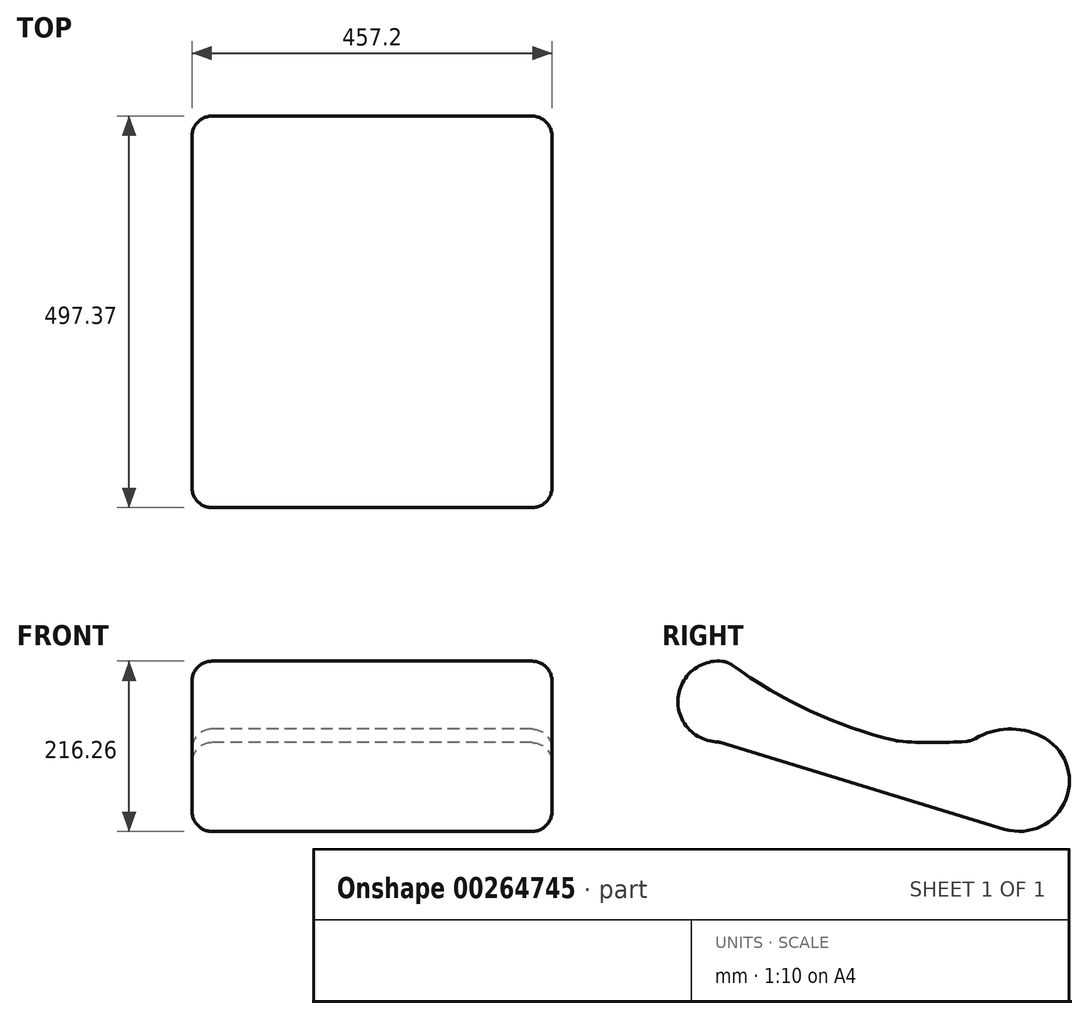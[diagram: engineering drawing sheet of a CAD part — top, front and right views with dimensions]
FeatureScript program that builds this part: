
annotation { "Feature Type Name" : "Feature", "Feature Type Description" : "" }
export const myFeature = defineFeature(function(context is Context, id is Id, definition is map)
    precondition{}
    {
        {
            var Q0;
            Q0=qCreatedBy(makeId("Right.planeOp"),FACE);
            var sketch = newSketch(context, id + "F0", { "sketchPlane" : qUnion([Q0])});
            skLineSegment(sketch, "E0", {"start": v(-410.9, 125.23) * mm, "end": v(-46.45, 14.16) * mm});
            skArc(sketch, "E1", {"start": v(-46.45, 14.16) * mm, "mid": v(31.4, 51.79) * mm, "end": v(0, 132.36) * mm});
            skArc(sketch, "E2", {"start": v(0, 132.36) * mm, "mid": v(-45.23, 141.16) * mm, "end": v(-88.83, 126.26) * mm});
            skArc(sketch, "E3", {"start": v(-183.23, 126.26) * mm, "mid": v(-136.03, 124.16) * mm, "end": v(-88.83, 126.26) * mm});
            skArc(sketch, "E4", {"start": v(-397.28, 225.96) * mm, "mid": v(-295.26, 165.36) * mm, "end": v(-183.23, 126.26) * mm});
            skArc(sketch, "E5", {"start": v(-397.28, 225.96) * mm, "mid": v(-461.09, 183.3) * mm, "end": v(-410.9, 125.23) * mm});
            skSolve(sketch);
        }
        {
            var Q0;
            Q0 = qSketchRegion(id + "F0", true);
            extrude(context, id + "F1", {"entities" : qUnion([Q0]), "endBound" : BoundingType.SYMMETRIC, "depth" : 457.2 * mm});
        }
        {
            var Q0;
            Q0=makeQuery(id+"F1.opExtrude","CAP_FACE",FACE,{"disambiguationData":[OSD([sQuery(id+"F0.wireOp",EDGE,"E0"),sQuery(id+"F0.wireOp",EDGE,"E1"),sQuery(id+"F0.wireOp",EDGE,"E2"),sQuery(id+"F0.wireOp",EDGE,"E3"),sQuery(id+"F0.wireOp",EDGE,"E4"),sQuery(id+"F0.wireOp",EDGE,"E5")])],"isStart":true});
            var Q1;
            Q1=makeQuery(id+"F1.opExtrude","CAP_FACE",FACE,{"disambiguationData":[OSD([sQuery(id+"F0.wireOp",EDGE,"E0"),sQuery(id+"F0.wireOp",EDGE,"E1"),sQuery(id+"F0.wireOp",EDGE,"E2"),sQuery(id+"F0.wireOp",EDGE,"E3"),sQuery(id+"F0.wireOp",EDGE,"E4"),sQuery(id+"F0.wireOp",EDGE,"E5")])],"isStart":false});
            var Q2;
            Q2=makeQuery(id+"F1.opExtrude","SWEPT_FACE",FACE,{"disambiguationData":[OSD([sQuery(id+"F0.wireOp",EDGE,"E3")])]});
            var Q3;
            Q3=makeQuery(id+"F1.opExtrude","SWEPT_FACE",FACE,{"disambiguationData":[OSD([sQuery(id+"F0.wireOp",EDGE,"E2")])]});
            var Q4;
            Q4=makeQuery(id+"F1.opExtrude","SWEPT_FACE",FACE,{"disambiguationData":[OSD([sQuery(id+"F0.wireOp",EDGE,"E4")])]});
            var Q5;
            Q5=makeQuery(id+"F1.opExtrude","SWEPT_FACE",FACE,{"disambiguationData":[OSD([sQuery(id+"F0.wireOp",EDGE,"E0")])]});
            var Q6;
            Q6=makeQuery(id+"F1.opExtrude","SWEPT_FACE",FACE,{"disambiguationData":[OSD([sQuery(id+"F0.wireOp",EDGE,"E1")])]});
            fillet(context, id + "F2", {"entities" : qUnion([Q0, Q1, Q2, Q3, Q4, Q5, Q6]), "radius" : 25.4 * mm, "tangentPropagation" : true, "allowEdgeOverflow" : false});
        }
    });
